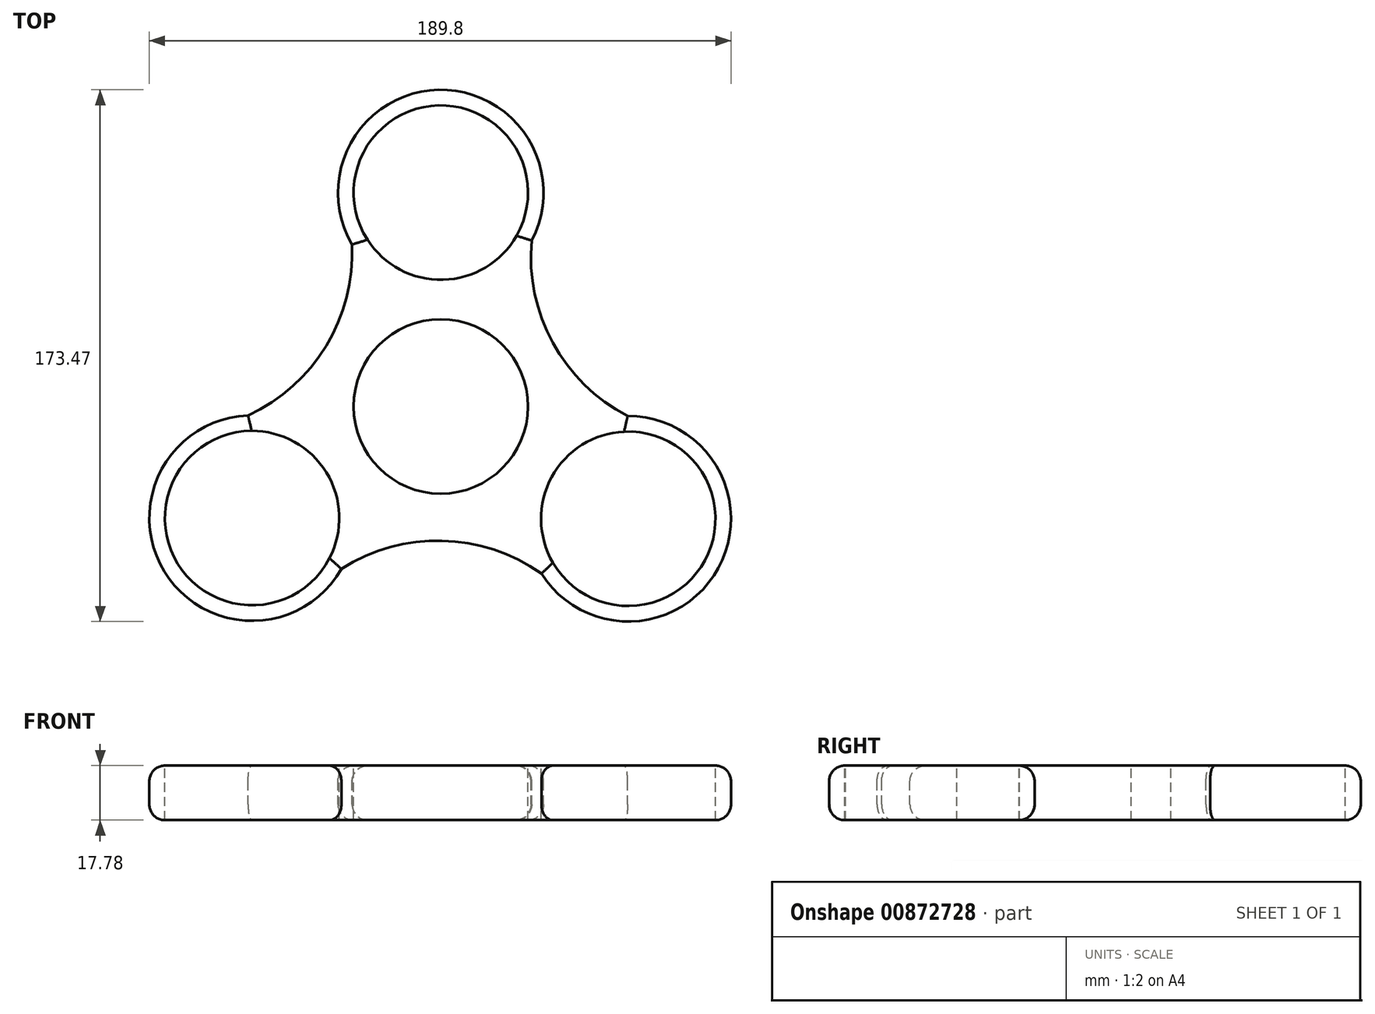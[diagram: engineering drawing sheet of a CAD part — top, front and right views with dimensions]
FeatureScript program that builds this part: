
annotation { "Feature Type Name" : "Feature", "Feature Type Description" : "" }
export const myFeature = defineFeature(function(context is Context, id is Id, definition is map)
    precondition{}
    {
        {
            var Q0;
            Q0=qCreatedBy(makeId("Top.planeOp"),FACE);
            var sketch = newSketch(context, id + "F0", { "sketchPlane" : qUnion([Q0])});
            skCircle(sketch, "E0", {"center": v(0, 0) * mm, "radius": 28.45 * mm});
            skCircle(sketch, "E1", {"center": v(0, 69.76) * mm, "radius": 28.45 * mm});
            skArc(sketch, "E2", {"start": v(29.67, 54.15) * mm, "mid": v(-0.75, 103.28) * mm, "end": v(-28.94, 52.84) * mm});
            skArc(sketch, "E3.1.0", {"start": v(32.82, -54.54) * mm, "mid": v(90.58, -52.76) * mm, "end": v(60.99, -3.12) * mm});
            skCircle(sketch, "E3.1.1", {"center": v(61.17, -36.65) * mm, "radius": 28.45 * mm});
            skArc(sketch, "E3.2.0", {"start": v(-62.88, -2.92) * mm, "mid": v(-90.22, -53.83) * mm, "end": v(-32.44, -53.02) * mm});
            skCircle(sketch, "E3.2.1", {"center": v(-61.57, -36.42) * mm, "radius": 28.45 * mm});
            skPoint(sketch, "E3.center", {"position": v(-0.13, -1.1) * mm});
            skLineSegment(sketch, "E3.anchor1", {"start": v(-0.13, -1.1) * mm, "end": v(0, 69.76) * mm, "construction": true});
            skArc(sketch, "E4", {"start": v(29.67, 54.15) * mm, "mid": v(36.57, 20.72) * mm, "end": v(60.99, -3.12) * mm});
            skArc(sketch, "E5.1.0", {"start": v(-62.88, -2.92) * mm, "mid": v(-37.39, 19.77) * mm, "end": v(-28.94, 52.84) * mm});
            skArc(sketch, "E5.2.0", {"start": v(32.82, -54.54) * mm, "mid": v(0.42, -43.8) * mm, "end": v(-32.44, -53.02) * mm});
            skSolve(sketch);
        }
        {
            var Q0;
            Q0=makeQuery(id+"F0.imprint","IMPRINT",FACE,{"disambiguationData":[TD([[makeQuery(id+"F0.imprint","IMPRINT",EDGE,{"derivedFrom":sQuery(id+"F0.wireOp",EDGE,"E0")}),-1.0]])]});
            extrude(context, id + "F1", {"entities" : qUnion([Q0]), "oppositeDirection" : true, "depth" : 17.78 * mm, "offsetDistance" : 25.4 * mm});
        }
        {
            var Q0;
            Q0=makeQuery(id+"F1.opExtrude","CAP_EDGE",EDGE,{"disambiguationData":[OSD([sQuery(id+"F0.wireOp",EDGE,"E5.2.0")])],"isStart":true});
            var Q1;
            Q1=makeQuery(id+"F1.opExtrude","CAP_EDGE",EDGE,{"disambiguationData":[OSD([sQuery(id+"F0.wireOp",EDGE,"E3.2.0")])],"isStart":true});
            var Q2;
            Q2=makeQuery(id+"F1.opExtrude","CAP_EDGE",EDGE,{"disambiguationData":[OSD([sQuery(id+"F0.wireOp",EDGE,"E5.1.0")])],"isStart":true});
            var Q3;
            Q3=makeQuery(id+"F1.opExtrude","CAP_EDGE",EDGE,{"disambiguationData":[OSD([sQuery(id+"F0.wireOp",EDGE,"E2")])],"isStart":true});
            var Q4;
            Q4=makeQuery(id+"F1.opExtrude","CAP_EDGE",EDGE,{"disambiguationData":[OSD([sQuery(id+"F0.wireOp",EDGE,"E3.1.0")])],"isStart":true});
            var Q5;
            Q5=makeQuery(id+"F1.opExtrude","CAP_EDGE",EDGE,{"disambiguationData":[OSD([sQuery(id+"F0.wireOp",EDGE,"E4")])],"isStart":true});
            var Q6;
            Q6=makeQuery(id+"F1.opExtrude","CAP_EDGE",EDGE,{"disambiguationData":[OSD([sQuery(id+"F0.wireOp",EDGE,"E3.1.0")])],"isStart":false});
            var Q7;
            Q7=makeQuery(id+"F1.opExtrude","CAP_EDGE",EDGE,{"disambiguationData":[OSD([sQuery(id+"F0.wireOp",EDGE,"E5.2.0")])],"isStart":false});
            var Q8;
            Q8=makeQuery(id+"F1.opExtrude","CAP_EDGE",EDGE,{"disambiguationData":[OSD([sQuery(id+"F0.wireOp",EDGE,"E3.2.0")])],"isStart":false});
            var Q9;
            Q9=makeQuery(id+"F1.opExtrude","CAP_EDGE",EDGE,{"disambiguationData":[OSD([sQuery(id+"F0.wireOp",EDGE,"E5.1.0")])],"isStart":false});
            var Q10;
            Q10=makeQuery(id+"F1.opExtrude","CAP_EDGE",EDGE,{"disambiguationData":[OSD([sQuery(id+"F0.wireOp",EDGE,"E2")])],"isStart":false});
            var Q11;
            Q11=makeQuery(id+"F1.opExtrude","CAP_EDGE",EDGE,{"disambiguationData":[OSD([sQuery(id+"F0.wireOp",EDGE,"E4")])],"isStart":false});
            fillet(context, id + "F2", {"entities" : qUnion([Q0, Q1, Q2, Q3, Q4, Q5, Q6, Q7, Q8, Q9, Q10, Q11]), "radius" : 5.08 * mm, "tangentPropagation" : true, "allowEdgeOverflow" : false});
        }
    });
